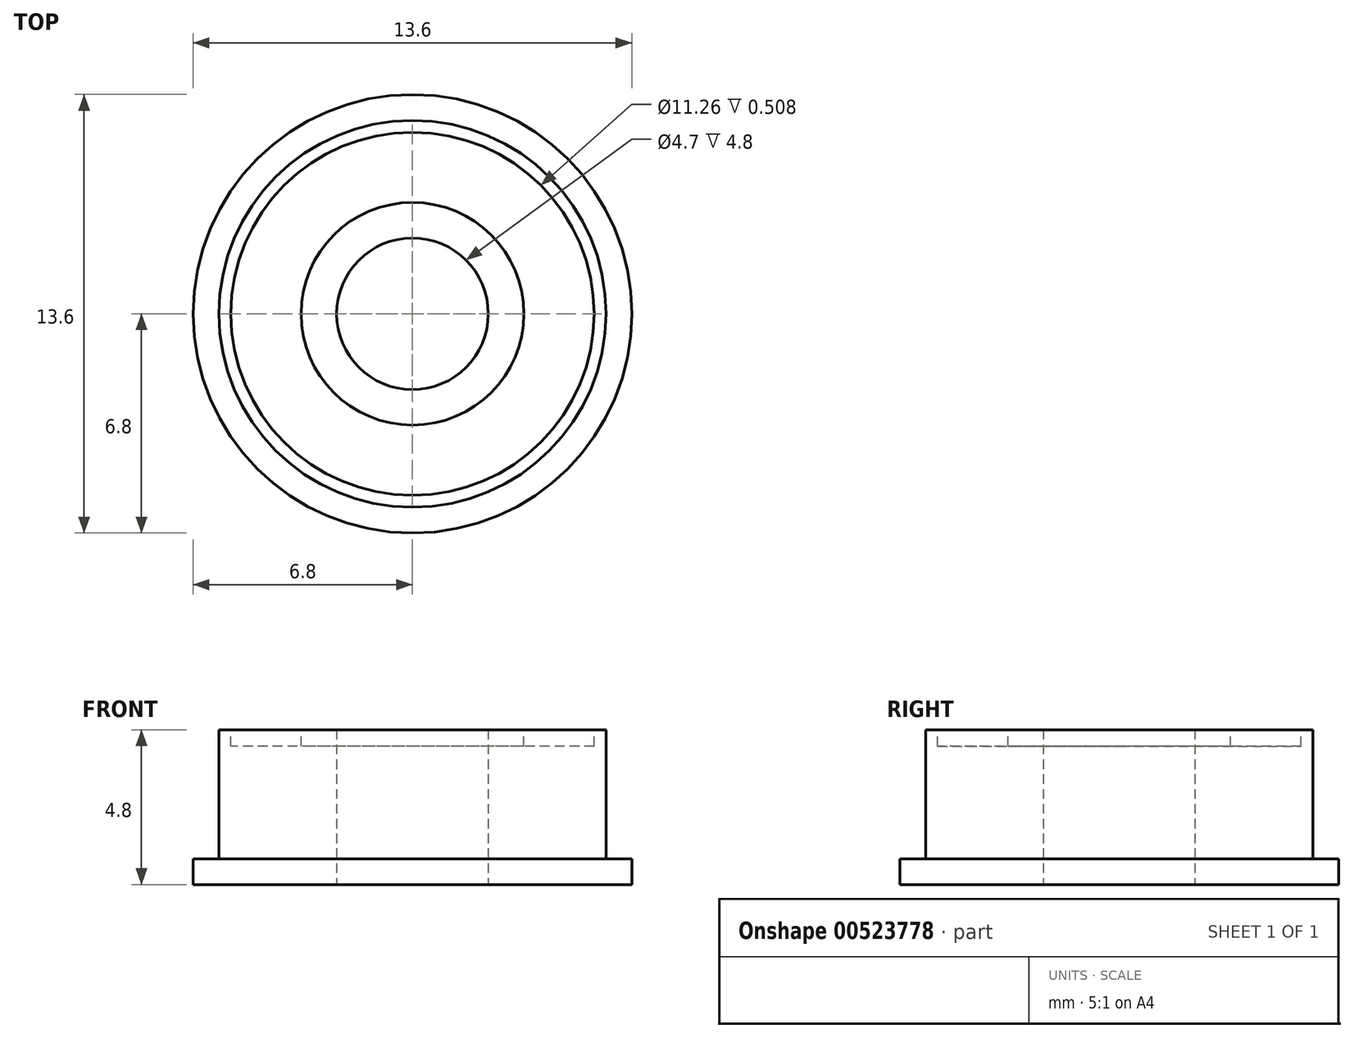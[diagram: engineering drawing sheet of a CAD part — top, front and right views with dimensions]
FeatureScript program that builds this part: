
annotation { "Feature Type Name" : "Feature", "Feature Type Description" : "" }
export const myFeature = defineFeature(function(context is Context, id is Id, definition is map)
    precondition{}
    {
        {
            var Q0;
            Q0=qCreatedBy(makeId("Top.planeOp"),FACE);
            var sketch = newSketch(context, id + "F0", { "sketchPlane" : qUnion([Q0])});
            skCircle(sketch, "E0", {"center": v(0, -1.4) * mm, "radius": 6.8 * mm});
            skSolve(sketch);
        }
        {
            var Q0;
            Q0=makeQuery(id+"F0.imprint","IMPRINT",FACE,{"disambiguationData":[TD([[makeQuery(id+"F0.imprint","IMPRINT",EDGE,{"derivedFrom":sQuery(id+"F0.wireOp",EDGE,"E0")}),1.0]])]});
            extrude(context, id + "F1", {"entities" : qUnion([Q0]), "depth" : 0.8 * mm, "offsetDistance" : 25.4 * mm});
        }
        {
            var Q0;
            Q0=makeQuery(id+"F1.opExtrude","CAP_FACE",FACE,{"disambiguationData":[OSD([sQuery(id+"F0.wireOp",EDGE,"E0")])],"isStart":false});
            var sketch = newSketch(context, id + "F2", { "sketchPlane" : qUnion([Q0])});
            skCircle(sketch, "E1", {"center": v(0, -1.4) * mm, "radius": 6 * mm});
            skSolve(sketch);
        }
        {
            var Q0;
            Q0=makeQuery(id+"F2.imprint","IMPRINT",FACE,{"disambiguationData":[TD([[makeQuery(id+"F2.imprint","IMPRINT",EDGE,{"derivedFrom":sQuery(id+"F2.wireOp",EDGE,"E1")}),1.0]])]});
            extrude(context, id + "F3", {"entities" : qUnion([Q0]), "operationType" : NewBodyOperationType.ADD, "depth" : 4 * mm, "offsetDistance" : 25.4 * mm});
        }
        {
            var Q0;
            Q0=makeQuery(id+"F3.opExtrude","CAP_FACE",FACE,{"disambiguationData":[OSD([sQuery(id+"F2.wireOp",EDGE,"E1")])],"isStart":false});
            var sketch = newSketch(context, id + "F4", { "sketchPlane" : qUnion([Q0])});
            skCircle(sketch, "E2", {"center": v(0, -1.4) * mm, "radius": 3 * mm});
            skSolve(sketch);
        }
        {
            var Q0;
            Q0=makeQuery(id+"F4.imprint","IMPRINT",FACE,{"disambiguationData":[TD([[makeQuery(id+"F4.imprint","IMPRINT",EDGE,{"derivedFrom":sQuery(id+"F4.wireOp",EDGE,"E2")}),1.0]])]});
            extrude(context, id + "F5", {"entities" : qUnion([Q0]), "operationType" : NewBodyOperationType.REMOVE, "oppositeDirection" : true, "depth" : 25.4 * mm, "offsetDistance" : 25.4 * mm});
        }
        {
            var Q0;
            Q0=makeQuery(id+"F3.opExtrude","CAP_FACE",FACE,{"disambiguationData":[OSD([sQuery(id+"F2.wireOp",EDGE,"E1")])],"isStart":false});
            var sketch = newSketch(context, id + "F6", { "sketchPlane" : qUnion([Q0])});
            skCircle(sketch, "E3", {"center": v(0, -1.4) * mm, "radius": 3.45 * mm});
            skCircle(sketch, "E4", {"center": v(0, -1.4) * mm, "radius": 5.63 * mm});
            skSolve(sketch);
        }
        {
            var Q0;
            Q0=makeQuery(id+"F6.imprint","IMPRINT",FACE,{"disambiguationData":[TD([[makeQuery(id+"F6.imprint","IMPRINT",EDGE,{"derivedFrom":sQuery(id+"F6.wireOp",EDGE,"E3")}),-1.0]])]});
            extrude(context, id + "F7", {"entities" : qUnion([Q0]), "operationType" : NewBodyOperationType.REMOVE, "oppositeDirection" : true, "depth" : 0.5 * mm, "offsetDistance" : 25.4 * mm});
        }
        {
            var Q0;
            Q0=makeQuery(id+"F1.opExtrude","CAP_FACE",FACE,{"disambiguationData":[OSD([sQuery(id+"F0.wireOp",EDGE,"E0")])],"isStart":true});
            var sketch = newSketch(context, id + "F8", { "sketchPlane" : qUnion([Q0])});
            skCircle(sketch, "E5", {"center": v(0, 1.4) * mm, "radius": 2.35 * mm});
            skCircle(sketch, "E6", {"center": v(0, 1.4) * mm, "radius": 3.11 * mm});
            skSolve(sketch);
        }
        {
            var Q0;
            Q0=makeQuery(id+"F8.imprint","IMPRINT",FACE,{"disambiguationData":[TD([[makeQuery(id+"F8.imprint","IMPRINT",EDGE,{"derivedFrom":sQuery(id+"F8.wireOp",EDGE,"E5")}),-1.0]])]});
            extrude(context, id + "F9", {"entities" : qUnion([Q0]), "operationType" : NewBodyOperationType.ADD, "oppositeDirection" : true, "depth" : 4.8 * mm, "offsetDistance" : 25.4 * mm});
        }
    });
